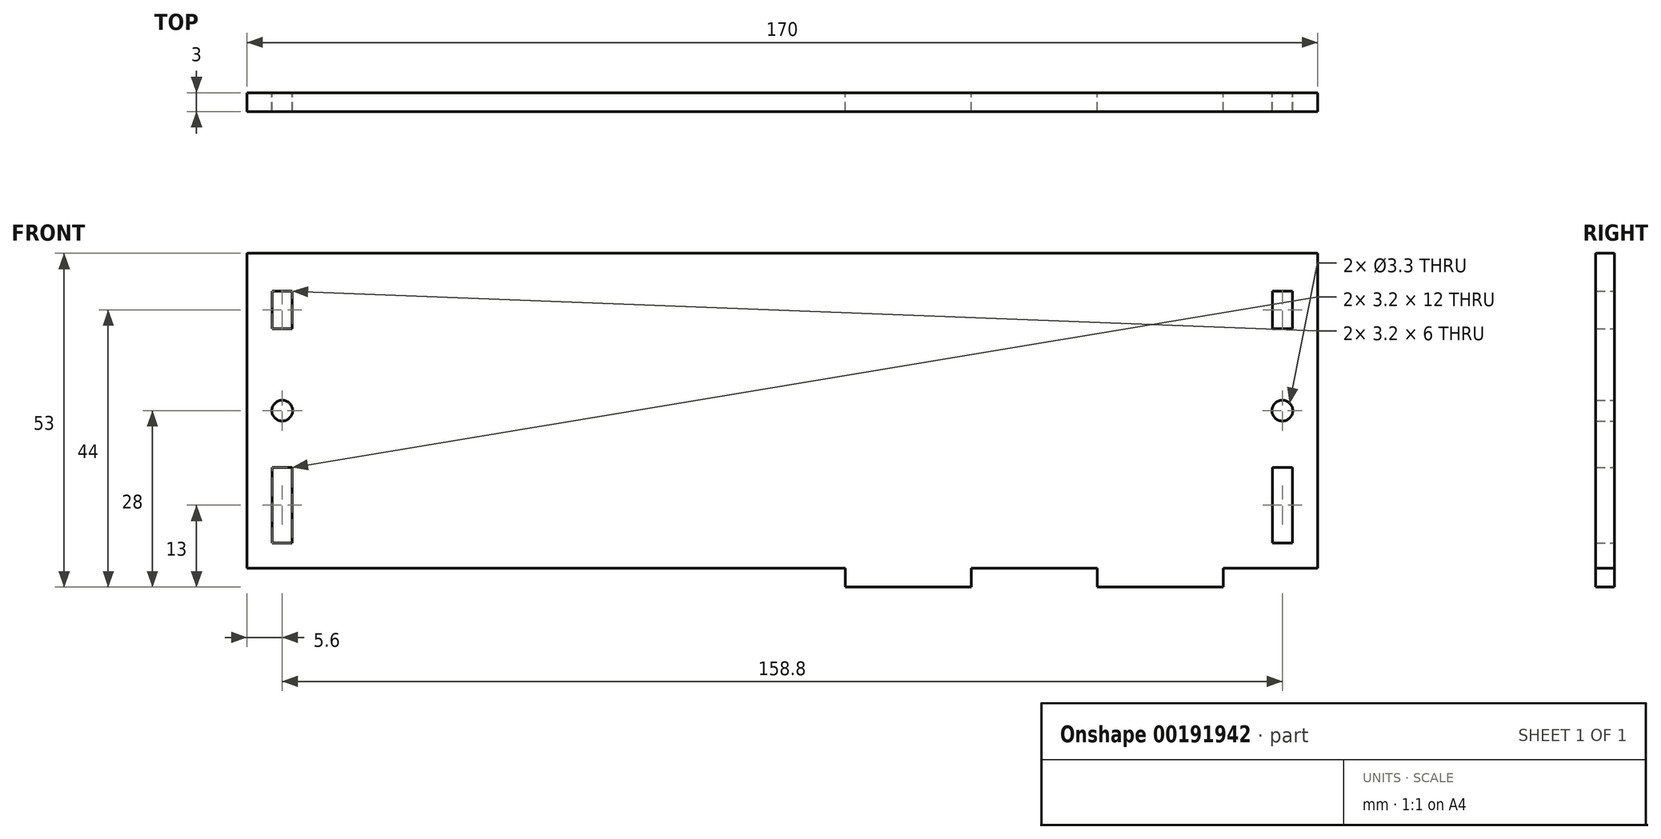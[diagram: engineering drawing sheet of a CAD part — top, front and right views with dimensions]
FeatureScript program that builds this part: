
annotation { "Feature Type Name" : "Feature", "Feature Type Description" : "" }
export const myFeature = defineFeature(function(context is Context, id is Id, definition is map)
    precondition{}
    {
        {
            var Q0;
            Q0=qCreatedBy(makeId("Front.planeOp"),FACE);
            var sketch = newSketch(context, id + "F0", { "sketchPlane" : qUnion([Q0])});
            skLineSegment(sketch, "E0.bottom", {"start": v(85, -25) * mm, "end": v(-85, -25) * mm});
            skLineSegment(sketch, "E0.top", {"start": v(85, 25) * mm, "end": v(-85, 25) * mm});
            skLineSegment(sketch, "E0.left", {"start": v(85, -25) * mm, "end": v(85, 25) * mm});
            skLineSegment(sketch, "E0.right", {"start": v(-85, -25) * mm, "end": v(-85, 25) * mm});
            skPoint(sketch, "E0.middle", {"position": v(0, 0) * mm});
            skLineSegment(sketch, "E1.bottom", {"start": v(-10, -25) * mm, "end": v(-30, -25) * mm});
            skLineSegment(sketch, "E1.top", {"start": v(-10, -28) * mm, "end": v(-30, -28) * mm});
            skLineSegment(sketch, "E1.left", {"start": v(-10, -25) * mm, "end": v(-10, -28) * mm});
            skLineSegment(sketch, "E1.right", {"start": v(-30, -25) * mm, "end": v(-30, -28) * mm});
            skLineSegment(sketch, "E2.bottom", {"start": v(-50, -25) * mm, "end": v(-70, -25) * mm});
            skLineSegment(sketch, "E2.top", {"start": v(-50, -28) * mm, "end": v(-70, -28) * mm});
            skLineSegment(sketch, "E2.left", {"start": v(-50, -25) * mm, "end": v(-50, -28) * mm});
            skLineSegment(sketch, "E2.right", {"start": v(-70, -25) * mm, "end": v(-70, -28) * mm});
            skLineSegment(sketch, "E3.MirrorCS", {"start": v(70, -25) * mm, "end": v(70, -28) * mm});
            skLineSegment(sketch, "E4.MirrorCS", {"start": v(50, -25) * mm, "end": v(50, -28) * mm});
            skLineSegment(sketch, "E5.MirrorCS", {"start": v(50, -28) * mm, "end": v(70, -28) * mm});
            skLineSegment(sketch, "E6.MirrorCS", {"start": v(50, -25) * mm, "end": v(70, -25) * mm});
            skLineSegment(sketch, "E7.MirrorCS", {"start": v(30, -25) * mm, "end": v(30, -28) * mm});
            skLineSegment(sketch, "E8.MirrorCS", {"start": v(10, -25) * mm, "end": v(10, -28) * mm});
            skLineSegment(sketch, "E9.MirrorCS", {"start": v(10, -25) * mm, "end": v(30, -25) * mm});
            skLineSegment(sketch, "E10.MirrorCS", {"start": v(10, -28) * mm, "end": v(30, -28) * mm});
            skLineSegment(sketch, "E11.bottom", {"start": v(-25, 25) * mm, "end": v(25, 25) * mm});
            skLineSegment(sketch, "E11.top", {"start": v(-25, 28) * mm, "end": v(25, 28) * mm});
            skLineSegment(sketch, "E11.left", {"start": v(-25, 25) * mm, "end": v(-25, 28) * mm});
            skLineSegment(sketch, "E11.right", {"start": v(25, 25) * mm, "end": v(25, 28) * mm});
            skLineSegment(sketch, "E12.bottom", {"start": v(-81, -21) * mm, "end": v(-77.8, -21) * mm});
            skLineSegment(sketch, "E12.top", {"start": v(-81, -9) * mm, "end": v(-77.8, -9) * mm});
            skLineSegment(sketch, "E12.left", {"start": v(-81, -21) * mm, "end": v(-81, -9) * mm});
            skLineSegment(sketch, "E12.right", {"start": v(-77.8, -21) * mm, "end": v(-77.8, -9) * mm});
            skLineSegment(sketch, "E13.bottom", {"start": v(-81, 19) * mm, "end": v(-77.8, 19) * mm});
            skLineSegment(sketch, "E13.top", {"start": v(-81, 13) * mm, "end": v(-77.8, 13) * mm});
            skLineSegment(sketch, "E13.left", {"start": v(-81, 19) * mm, "end": v(-81, 13) * mm});
            skLineSegment(sketch, "E13.right", {"start": v(-77.8, 19) * mm, "end": v(-77.8, 13) * mm});
            skLineSegment(sketch, "E14.MirrorCS", {"start": v(81, -21) * mm, "end": v(77.8, -21) * mm});
            skLineSegment(sketch, "E15.MirrorCS", {"start": v(81, -9) * mm, "end": v(77.8, -9) * mm});
            skLineSegment(sketch, "E16.MirrorCS", {"start": v(81, 19) * mm, "end": v(77.8, 19) * mm});
            skLineSegment(sketch, "E17.MirrorCS", {"start": v(81, 13) * mm, "end": v(77.8, 13) * mm});
            skLineSegment(sketch, "E18.MirrorCS", {"start": v(81, 19) * mm, "end": v(81, 13) * mm});
            skLineSegment(sketch, "E19.MirrorCS", {"start": v(77.8, -21) * mm, "end": v(77.8, -9) * mm});
            skLineSegment(sketch, "E20.MirrorCS", {"start": v(81, -21) * mm, "end": v(81, -9) * mm});
            skLineSegment(sketch, "E21.MirrorCS", {"start": v(77.8, 19) * mm, "end": v(77.8, 13) * mm});
            skPoint(sketch, "E22", {"position": v(-79.4, -9) * mm});
            skCircle(sketch, "E23", {"center": v(-79.4, 0) * mm, "radius": 1.65 * mm});
            skCircle(sketch, "E24.MirrorC", {"center": v(79.4, 0) * mm, "radius": 1.65 * mm});
            skSolve(sketch);
        }
        {
            var Q0;
            {var subQ8=sQuery(id+"F0.wireOp",EDGE,"E0.left");Q0=makeQuery(id+"F0.imprint","IMPRINT",FACE,{"disambiguationData":[TD([[makeQuery(id+"F0.imprint","IMPRINT",EDGE,{"derivedFrom":subQ8}),1.0]])]});}
            var Q1;
            Q1=makeQuery(id+"F0.imprint","IMPRINT",FACE,{"disambiguationData":[TD([[makeQuery(id+"F0.imprint","IMPRINT",EDGE,{"derivedFrom":sQuery(id+"F0.wireOp",EDGE,"E11.bottom")}),1.0]])]});
            var Q2;
            Q2=makeQuery(id+"F0.imprint","IMPRINT",FACE,{"disambiguationData":[TD([[makeQuery(id+"F0.imprint","IMPRINT",EDGE,{"derivedFrom":sQuery(id+"F0.wireOp",EDGE,"E2.bottom")}),1.0]])]});
            var Q3;
            Q3=makeQuery(id+"F0.imprint","IMPRINT",FACE,{"disambiguationData":[TD([[makeQuery(id+"F0.imprint","IMPRINT",EDGE,{"derivedFrom":sQuery(id+"F0.wireOp",EDGE,"E1.bottom")}),1.0]])]});
            var Q4;
            Q4=makeQuery(id+"F0.imprint","IMPRINT",FACE,{"disambiguationData":[TD([[makeQuery(id+"F0.imprint","IMPRINT",EDGE,{"derivedFrom":sQuery(id+"F0.wireOp",EDGE,"E7.MirrorCS")}),-1.0]])]});
            var Q5;
            Q5=makeQuery(id+"F0.imprint","IMPRINT",FACE,{"disambiguationData":[TD([[makeQuery(id+"F0.imprint","IMPRINT",EDGE,{"derivedFrom":sQuery(id+"F0.wireOp",EDGE,"E3.MirrorCS")}),-1.0]])]});
            extrude(context, id + "F1", {"entities" : qUnion([Q0, Q1, Q2, Q3, Q4, Q5]), "depth" : 3 * mm});
        }
    });
